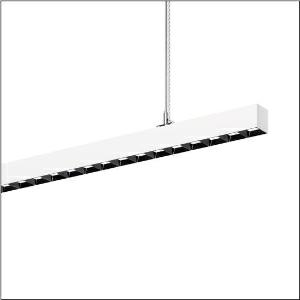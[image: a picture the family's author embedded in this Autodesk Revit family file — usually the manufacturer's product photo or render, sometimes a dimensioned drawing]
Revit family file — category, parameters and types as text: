
# Revit family: silica_r__21_51mx34dc3dwb_cbfc
name_source: partatom
category: Lighting Fixtures
units: mm (PartAtom-declared; Revit-internal decimal feet)

## family parameters
Cut with Voids When Loaded = No
Host = Face
Light Source = No
Part Type = Normal
Room Calculation Point = No
Round Connector Dimension = Use Diameter
Shared = No

## types (1)
- --- (1 x LED, 19200 lm, 129.1 W, 3000K)
    Apparent Load = 129 VA
    CIE Flux Codes = 74 94 99 56 100
    Color Rendering = 80
    Color Temperature = 3000K
    Default Elevation = 1800 mm
    Description = Silica® 21, office luminaire, primary light control with darklight reflector, of PMMA, black, light emission: direct/indirect distribution, primary light characteristic: asymmetric, installation type: suspended mounting, LED, rated luminous flux: 19.200lm, luminous efficacy: 149lm/W, light colour: 830, colour temperature: 3000K, with terminal, 3+2-pole, max. 2.5mm², mains connection: 220..240V, AC, 50/60Hz, rated input power: 129.1W, luminaire housing, of aluminium, traffic white (RAL 9016), length: 3.004mm, width: 53mm, height: 53mm, protection rating (complete): IP20, insulation class (complete): insulation class I (protective earthing), certification: CE, permissible operating ambient temperature: 0..+35°C, standard: EN 50419, packaging unit: 1 piece
    Height = 53 mm
    Lamp = 1 x LED
    Lamp Light Flux = 19200 lm
    Lamp Power = 129.1 W
    Lamp count = 1
    Length = 3004 mm
    Luminous efficacy = 149 lm/W
    Manufacturer = Siteco
    ModVariant = No
    Model = 51MX34DC3DWB
    Mounting Place = Ceiling
    Mounting Type = Pendant
    Number of Poles = 1
    OnlyDefault = Yes
    Power Factor = 1
    Product Name = Silica® 21
    Product group = office luminaire | ceiling pendant
    ProductGroupID = 902
    Protection Class = Protection class I
    Protection Degree = IP 20
    RLX_Detail_Level = 1
    RLX_Emergency_Light_Flux = 0 lm
    RLX_Emergency_Type = 0
    RLX_Emergency_Type_DB = No
    RlxData = <blob elided: 65773 chars, md5=425c5bf9>
    Socket = socket
    Standby Power = 0 W
    System Light Flux = 19200 lm
    System Power = 129 W
    Type Comments = factory setting: luminous flux: 100 % | dim-lin: 254 | 448 mA
    Type Image = l_1313619.jpg
    URL = http://relux.com
    VarID = @adj_069115
    Voltage = 0 V
    Weight = 0.00 kg
    Width = 53 mm

## geometry (parser evidence)
native form markers: Blend x4, Sweep x13
no freeform markers — native parametric forms only
